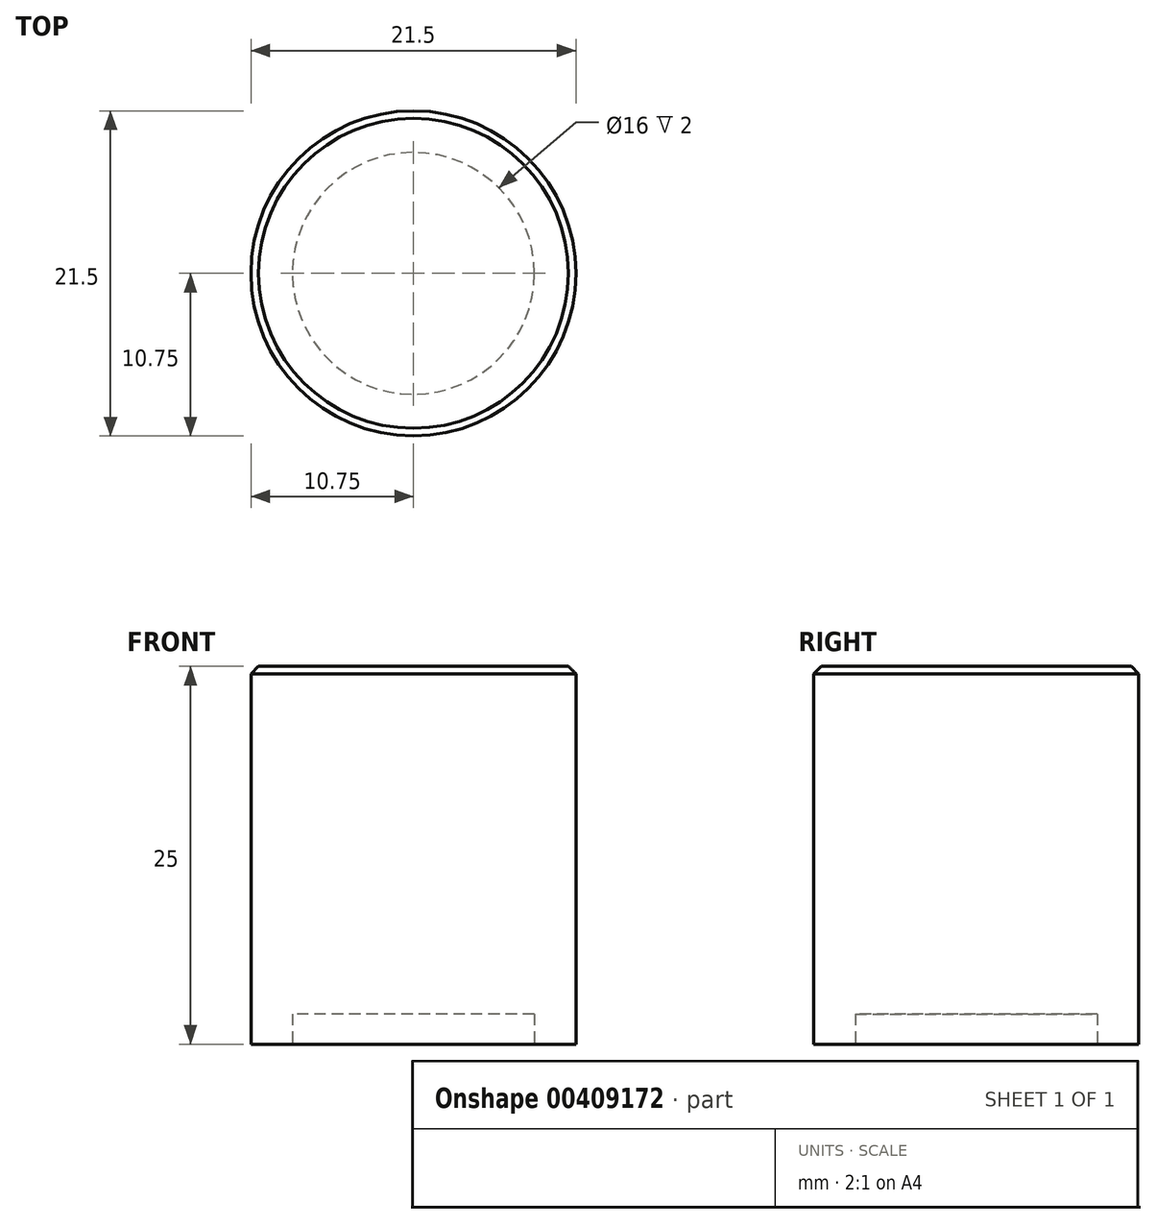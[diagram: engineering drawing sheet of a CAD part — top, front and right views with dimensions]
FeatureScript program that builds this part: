
annotation { "Feature Type Name" : "Feature", "Feature Type Description" : "" }
export const myFeature = defineFeature(function(context is Context, id is Id, definition is map)
    precondition{}
    {
        {
            var Q0;
            Q0=qCreatedBy(makeId("Top.planeOp"),FACE);
            var sketch = newSketch(context, id + "F0", { "sketchPlane" : qUnion([Q0])});
            skCircle(sketch, "E0", {"center": v(0, 0) * mm, "radius": 10.75 * mm});
            skCircle(sketch, "E1", {"center": v(0, 0) * mm, "radius": 8 * mm});
            skSolve(sketch);
        }
        {
            var Q0;
            Q0=makeQuery(id+"F0.imprint","IMPRINT",FACE,{"disambiguationData":[TD([[makeQuery(id+"F0.imprint","IMPRINT",EDGE,{"derivedFrom":sQuery(id+"F0.wireOp",EDGE,"E1")}),1.0]])]});
            var Q1;
            Q1=makeQuery(id+"F0.imprint","IMPRINT",FACE,{"disambiguationData":[TD([[makeQuery(id+"F0.imprint","IMPRINT",EDGE,{"derivedFrom":sQuery(id+"F0.wireOp",EDGE,"E0")}),1.0]])]});
            extrude(context, id + "F1", {"entities" : qUnion([Q0, Q1]), "depth" : 25 * mm});
        }
        {
            var Q0;
            Q0=makeQuery(id+"F0.imprint","IMPRINT",FACE,{"disambiguationData":[TD([[makeQuery(id+"F0.imprint","IMPRINT",EDGE,{"derivedFrom":sQuery(id+"F0.wireOp",EDGE,"E1")}),1.0]])]});
            extrude(context, id + "F2", {"entities" : qUnion([Q0]), "operationType" : NewBodyOperationType.REMOVE, "depth" : 2 * mm});
        }
        {
            var Q0;
            Q0=makeQuery(id+"F1.opExtrude","CAP_EDGE",EDGE,{"disambiguationData":[OSD([sQuery(id+"F0.wireOp",EDGE,"E0")])],"isStart":false});
            chamfer(context, id + "F3", {"entities" : qUnion([Q0]), "width" : 0.5 * mm, "tangentPropagation" : true});
        }
    });
